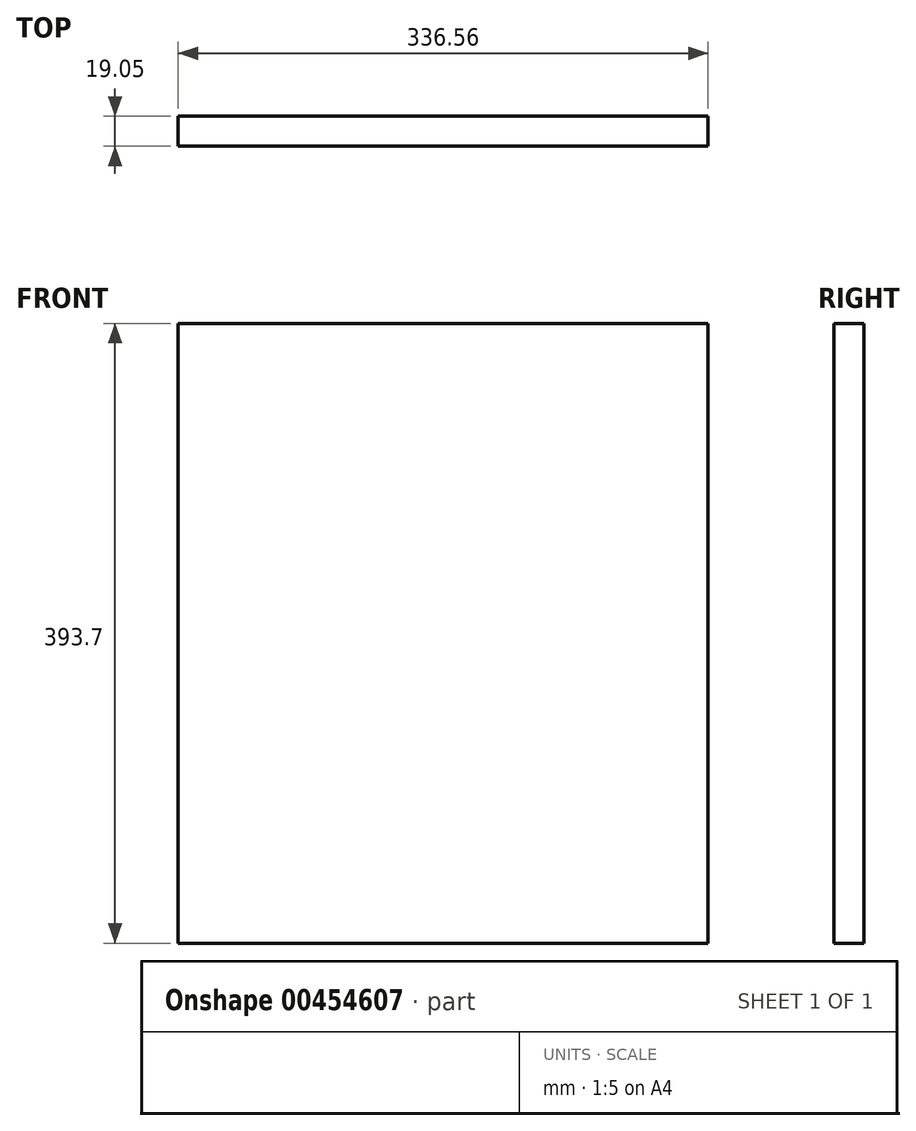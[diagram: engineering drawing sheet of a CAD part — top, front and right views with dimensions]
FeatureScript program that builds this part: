
annotation { "Feature Type Name" : "Feature", "Feature Type Description" : "" }
export const myFeature = defineFeature(function(context is Context, id is Id, definition is map)
    precondition{}
    {
        {
            var Q0;
            Q0=qCreatedBy(makeId("Front.planeOp"),FACE);
            var sketch = newSketch(context, id + "F0", { "sketchPlane" : qUnion([Q0])});
            skLineSegment(sketch, "E0.bottom", {"start": v(168.27, 196.85) * mm, "end": v(-168.28, 196.85) * mm});
            skLineSegment(sketch, "E0.top", {"start": v(168.28, -196.85) * mm, "end": v(-168.27, -196.85) * mm});
            skLineSegment(sketch, "E0.left", {"start": v(168.27, 196.85) * mm, "end": v(168.28, -196.85) * mm});
            skLineSegment(sketch, "E0.right", {"start": v(-168.28, 196.85) * mm, "end": v(-168.27, -196.85) * mm});
            skPoint(sketch, "E0.middle", {"position": v(0, 0) * mm});
            skSolve(sketch);
        }
        {
            var Q0;
            Q0=qSketchRegion(id+"F0",true);
            extrude(context, id + "F1", {"entities" : qUnion([Q0]), "depth" : 19.05 * mm});
        }
    });
